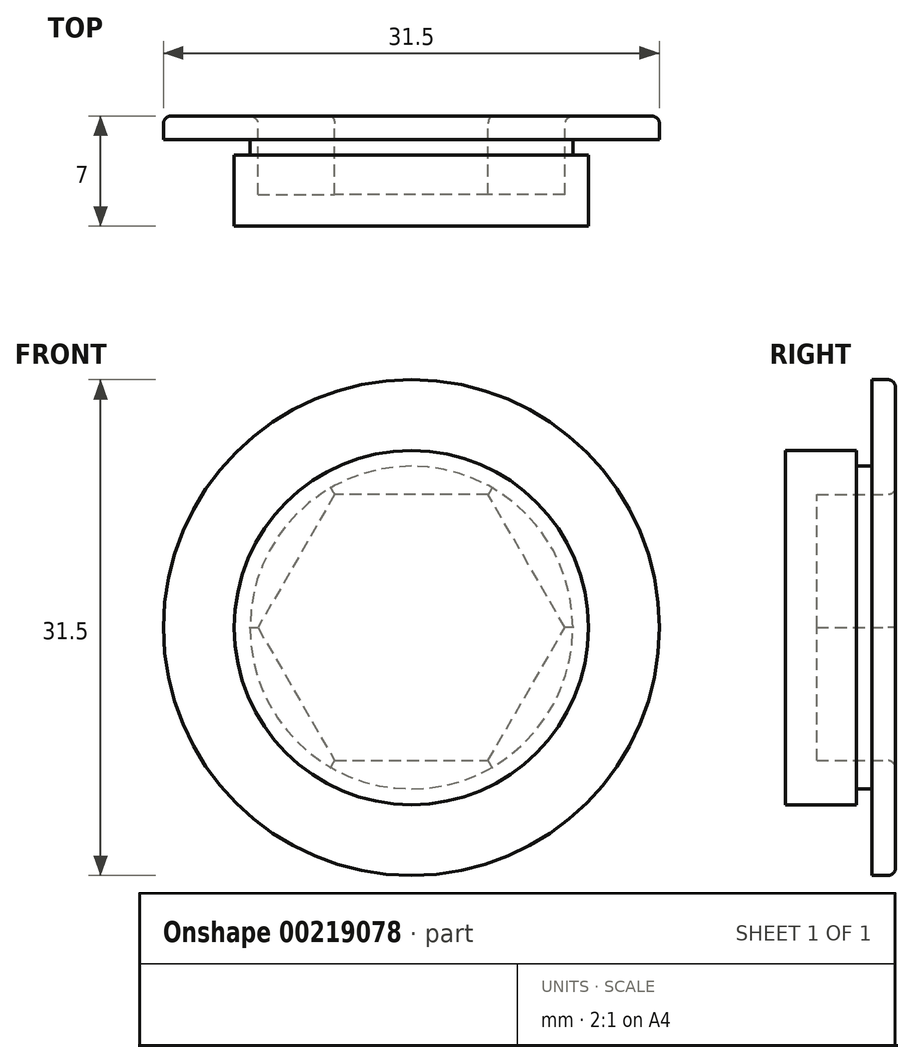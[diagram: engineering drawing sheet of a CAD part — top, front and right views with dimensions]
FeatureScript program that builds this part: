
annotation { "Feature Type Name" : "Feature", "Feature Type Description" : "" }
export const myFeature = defineFeature(function(context is Context, id is Id, definition is map)
    precondition{}
    {
        {
            var Q0;
            Q0=qCreatedBy(makeId("Front.planeOp"),FACE);
            var sketch = newSketch(context, id + "F0", { "sketchPlane" : qUnion([Q0])});
            skCircle(sketch, "E0", {"center": v(0, 0) * mm, "radius": 11.25 * mm});
            skSolve(sketch);
        }
        {
            var Q0;
            Q0=makeQuery(id+"F0.imprint","IMPRINT",FACE,{"disambiguationData":[TD([[makeQuery(id+"F0.imprint","IMPRINT",EDGE,{"derivedFrom":sQuery(id+"F0.wireOp",EDGE,"E0")}),1.0]])]});
            extrude(context, id + "F1", {"entities" : qUnion([Q0]), "depth" : 4.5 * mm});
        }
        {
            var Q0;
            Q0=makeQuery(id+"F1.opExtrude","CAP_FACE",FACE,{"disambiguationData":[OSD([sQuery(id+"F0.wireOp",EDGE,"E0")])],"isStart":true});
            var sketch = newSketch(context, id + "F2", { "sketchPlane" : qUnion([Q0])});
            skCircle(sketch, "E1", {"center": v(0, 0) * mm, "radius": 10.25 * mm});
            skSolve(sketch);
        }
        {
            var Q0;
            Q0=makeQuery(id+"F2.imprint","IMPRINT",FACE,{"disambiguationData":[TD([[makeQuery(id+"F2.imprint","IMPRINT",EDGE,{"derivedFrom":sQuery(id+"F2.wireOp",EDGE,"E1")}),1.0]])]});
            extrude(context, id + "F3", {"entities" : qUnion([Q0]), "operationType" : NewBodyOperationType.ADD, "depth" : 1 * mm});
        }
        {
            var Q0;
            Q0=makeQuery(id+"F3.opExtrude","CAP_FACE",FACE,{"disambiguationData":[OSD([sQuery(id+"F2.wireOp",EDGE,"E1")])],"isStart":false});
            var sketch = newSketch(context, id + "F4", { "sketchPlane" : qUnion([Q0])});
            skCircle(sketch, "E2", {"center": v(0, 0) * mm, "radius": 15.75 * mm});
            skSolve(sketch);
        }
        {
            var Q0;
            Q0 = qSketchRegion(id + "F4", true);
            extrude(context, id + "F5", {"entities" : qUnion([Q0]), "operationType" : NewBodyOperationType.ADD, "depth" : 1.5 * mm});
        }
        {
            var Q0;
            Q0=makeQuery(id+"F5.opExtrude","CAP_FACE",FACE,{"disambiguationData":[OSD([sQuery(id+"F4.wireOp",EDGE,"E2")])],"isStart":false});
            var sketch = newSketch(context, id + "F6", { "sketchPlane" : qUnion([Q0])});
            skCircle(sketch, "E3.cCircle", {"center": v(0, 0) * mm, "radius": 8.44 * mm, "construction": true});
            skLineSegment(sketch, "E3.0", {"start": v(-4.88, 8.44) * mm, "end": v(4.88, 8.44) * mm});
            skLineSegment(sketch, "E3.1", {"start": v(4.87, 8.44) * mm, "end": v(9.75, 0) * mm});
            skLineSegment(sketch, "E3.2", {"start": v(9.75, 0) * mm, "end": v(4.87, -8.44) * mm});
            skLineSegment(sketch, "E3.3", {"start": v(4.88, -8.44) * mm, "end": v(-4.87, -8.44) * mm});
            skLineSegment(sketch, "E3.4", {"start": v(-4.87, -8.44) * mm, "end": v(-9.75, 0) * mm});
            skLineSegment(sketch, "E3.5", {"start": v(-9.75, 0) * mm, "end": v(-4.87, 8.44) * mm});
            skPoint(sketch, "E3.0.midPoint", {"position": v(0, 8.44) * mm});
            skSolve(sketch);
        }
        {
            var Q0;
            Q0=makeQuery(id+"F6.imprint","IMPRINT",FACE,{"disambiguationData":[TD([[makeQuery(id+"F6.imprint","IMPRINT",EDGE,{"derivedFrom":sQuery(id+"F6.wireOp",EDGE,"E3.0")}),-1.0]])]});
            extrude(context, id + "F7", {"entities" : qUnion([Q0]), "operationType" : NewBodyOperationType.REMOVE, "oppositeDirection" : true, "depth" : 5 * mm});
        }
        {
            var Q0;
            Q0=makeQuery(id+"F5.opExtrude","CAP_FACE",FACE,{"disambiguationData":[OSD([sQuery(id+"F4.wireOp",EDGE,"E2")])],"isStart":false});
            fillet(context, id + "F8", {"entities" : qUnion([Q0]), "radius" : 0.5 * mm, "tangentPropagation" : true, "allowEdgeOverflow" : false});
        }
    });
